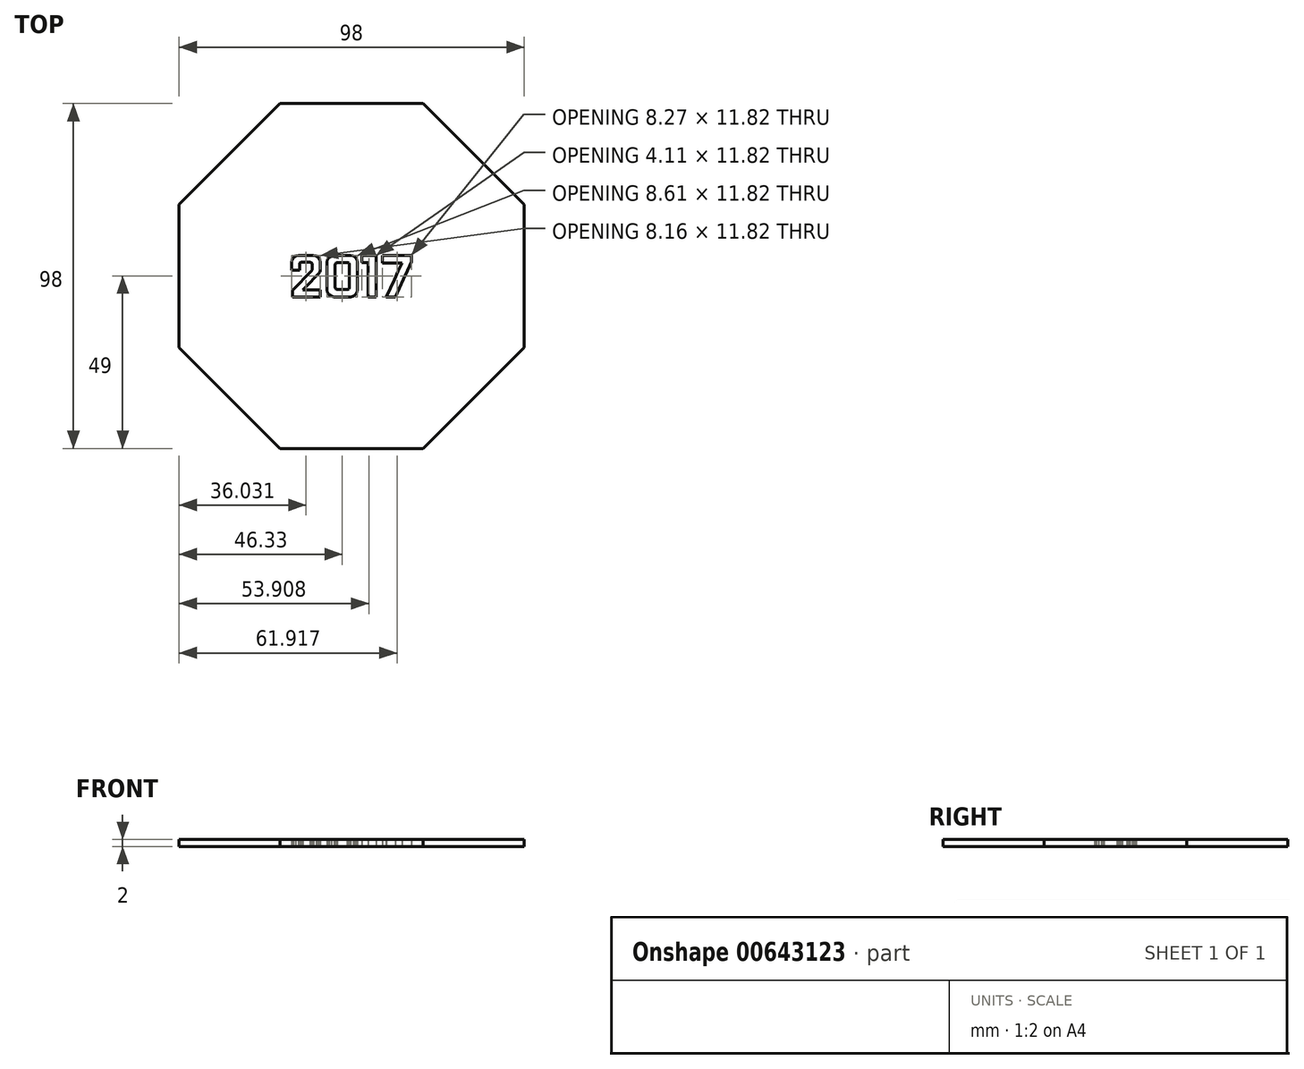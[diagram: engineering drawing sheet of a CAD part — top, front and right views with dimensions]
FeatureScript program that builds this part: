
annotation { "Feature Type Name" : "Feature", "Feature Type Description" : "" }
export const myFeature = defineFeature(function(context is Context, id is Id, definition is map)
    precondition{}
    {
        {
            var Q0;
            Q0=qCreatedBy(makeId("Top.planeOp"),FACE);
            var sketch = newSketch(context, id + "F0", { "sketchPlane" : qUnion([Q0])});
            skLineSegment(sketch, "E0", {"start": v(20.3, 49) * mm, "end": v(-20.3, 49) * mm});
            skLineSegment(sketch, "E1", {"start": v(-20.3, 49) * mm, "end": v(-49, 20.3) * mm});
            skLineSegment(sketch, "E2", {"start": v(-49, 20.3) * mm, "end": v(-49, -20.3) * mm});
            skLineSegment(sketch, "E3", {"start": v(-49, -20.3) * mm, "end": v(-20.3, -49) * mm});
            skLineSegment(sketch, "E4", {"start": v(-20.3, -49) * mm, "end": v(20.3, -49) * mm});
            skLineSegment(sketch, "E5", {"start": v(20.3, -49) * mm, "end": v(49, -20.3) * mm});
            skLineSegment(sketch, "E6", {"start": v(49, -20.3) * mm, "end": v(49, 20.3) * mm});
            skLineSegment(sketch, "E7", {"start": v(49, 20.3) * mm, "end": v(20.3, 49) * mm});
            skLineSegment(sketch, "E8", {"start": v(-17.05, 1.72) * mm, "end": v(-16.48, 1.72) * mm});
            skLineSegment(sketch, "E9", {"start": v(-16.48, 1.72) * mm, "end": v(-15.9, 1.72) * mm});
            skLineSegment(sketch, "E10", {"start": v(-15.9, 1.72) * mm, "end": v(-15.33, 1.72) * mm});
            skLineSegment(sketch, "E11", {"start": v(-15.33, 1.72) * mm, "end": v(-14.76, 1.72) * mm});
            skLineSegment(sketch, "E12", {"start": v(-12.97, 5.9) * mm, "end": v(-14.02, 5.9) * mm});
            skLineSegment(sketch, "E13", {"start": v(-14.02, 5.9) * mm, "end": v(-15.07, 5.9) * mm});
            skLineSegment(sketch, "E14", {"start": v(-15.07, 5.9) * mm, "end": v(-15.84, 5.75) * mm});
            skLineSegment(sketch, "E15", {"start": v(-15.84, 5.75) * mm, "end": v(-16.47, 5.33) * mm});
            skLineSegment(sketch, "E16", {"start": v(-16.47, 5.33) * mm, "end": v(-16.9, 4.7) * mm});
            skLineSegment(sketch, "E17", {"start": v(-16.9, 4.7) * mm, "end": v(-17.05, 3.93) * mm});
            skLineSegment(sketch, "E18", {"start": v(-17.05, 3.93) * mm, "end": v(-17.05, 3.38) * mm});
            skLineSegment(sketch, "E19", {"start": v(-17.05, 3.38) * mm, "end": v(-17.05, 2.82) * mm});
            skLineSegment(sketch, "E20", {"start": v(-17.05, 2.82) * mm, "end": v(-17.05, 2.27) * mm});
            skLineSegment(sketch, "E21", {"start": v(-17.05, 2.27) * mm, "end": v(-17.05, 1.72) * mm});
            skLineSegment(sketch, "E22", {"start": v(-8.89, 2.95) * mm, "end": v(-8.89, 3.44) * mm});
            skLineSegment(sketch, "E23", {"start": v(-8.89, 3.44) * mm, "end": v(-8.89, 3.93) * mm});
            skLineSegment(sketch, "E24", {"start": v(-8.89, 3.93) * mm, "end": v(-9.04, 4.7) * mm});
            skLineSegment(sketch, "E25", {"start": v(-9.04, 4.7) * mm, "end": v(-9.47, 5.33) * mm});
            skLineSegment(sketch, "E26", {"start": v(-9.47, 5.33) * mm, "end": v(-10.1, 5.75) * mm});
            skLineSegment(sketch, "E27", {"start": v(-10.1, 5.75) * mm, "end": v(-10.86, 5.9) * mm});
            skLineSegment(sketch, "E28", {"start": v(-10.86, 5.9) * mm, "end": v(-11.92, 5.9) * mm});
            skLineSegment(sketch, "E29", {"start": v(-11.92, 5.9) * mm, "end": v(-12.97, 5.9) * mm});
            skLineSegment(sketch, "E30", {"start": v(-10, 0.03) * mm, "end": v(-9.58, 0.45) * mm});
            skLineSegment(sketch, "E31", {"start": v(-9.58, 0.45) * mm, "end": v(-9.3, 0.77) * mm});
            skLineSegment(sketch, "E32", {"start": v(-9.3, 0.77) * mm, "end": v(-9.08, 1.14) * mm});
            skLineSegment(sketch, "E33", {"start": v(-9.08, 1.14) * mm, "end": v(-8.94, 1.54) * mm});
            skLineSegment(sketch, "E34", {"start": v(-8.94, 1.54) * mm, "end": v(-8.89, 1.96) * mm});
            skLineSegment(sketch, "E35", {"start": v(-8.89, 1.96) * mm, "end": v(-8.89, 2.45) * mm});
            skLineSegment(sketch, "E36", {"start": v(-8.89, 2.45) * mm, "end": v(-8.89, 2.95) * mm});
            skLineSegment(sketch, "E37", {"start": v(-13.83, -3.9) * mm, "end": v(-12.77, -2.81) * mm});
            skLineSegment(sketch, "E38", {"start": v(-12.77, -2.81) * mm, "end": v(-11.7, -1.72) * mm});
            skLineSegment(sketch, "E39", {"start": v(-11.7, -1.72) * mm, "end": v(-10.64, -0.64) * mm});
            skLineSegment(sketch, "E40", {"start": v(-10.64, -0.64) * mm, "end": v(-10, 0.03) * mm});
            skLineSegment(sketch, "E41", {"start": v(-8.89, -3.9) * mm, "end": v(-10.12, -3.9) * mm});
            skLineSegment(sketch, "E42", {"start": v(-10.12, -3.9) * mm, "end": v(-11.36, -3.9) * mm});
            skLineSegment(sketch, "E43", {"start": v(-11.36, -3.9) * mm, "end": v(-12.6, -3.9) * mm});
            skLineSegment(sketch, "E44", {"start": v(-12.6, -3.9) * mm, "end": v(-13.83, -3.9) * mm});
            skLineSegment(sketch, "E45", {"start": v(-8.89, -5.9) * mm, "end": v(-8.89, -5.4) * mm});
            skLineSegment(sketch, "E46", {"start": v(-8.89, -5.4) * mm, "end": v(-8.89, -4.9) * mm});
            skLineSegment(sketch, "E47", {"start": v(-8.89, -4.9) * mm, "end": v(-8.89, -4.4) * mm});
            skLineSegment(sketch, "E48", {"start": v(-8.89, -4.4) * mm, "end": v(-8.89, -3.9) * mm});
            skLineSegment(sketch, "E49", {"start": v(-16.8, -5.9) * mm, "end": v(-14.81, -5.9) * mm});
            skLineSegment(sketch, "E50", {"start": v(-14.81, -5.9) * mm, "end": v(-12.84, -5.9) * mm});
            skLineSegment(sketch, "E51", {"start": v(-12.84, -5.9) * mm, "end": v(-10.86, -5.9) * mm});
            skLineSegment(sketch, "E52", {"start": v(-10.86, -5.9) * mm, "end": v(-8.89, -5.9) * mm});
            skLineSegment(sketch, "E53", {"start": v(-16.8, -4.02) * mm, "end": v(-16.8, -4.5) * mm});
            skLineSegment(sketch, "E54", {"start": v(-16.8, -4.5) * mm, "end": v(-16.8, -4.97) * mm});
            skLineSegment(sketch, "E55", {"start": v(-16.8, -4.97) * mm, "end": v(-16.8, -5.44) * mm});
            skLineSegment(sketch, "E56", {"start": v(-16.8, -5.44) * mm, "end": v(-16.8, -5.9) * mm});
            skLineSegment(sketch, "E57", {"start": v(-11.18, 2.65) * mm, "end": v(-11.18, 2.32) * mm});
            skLineSegment(sketch, "E58", {"start": v(-11.18, 2.32) * mm, "end": v(-11.18, 2) * mm});
            skLineSegment(sketch, "E59", {"start": v(-11.18, 2) * mm, "end": v(-11.19, 1.87) * mm});
            skLineSegment(sketch, "E60", {"start": v(-11.19, 1.87) * mm, "end": v(-11.23, 1.76) * mm});
            skLineSegment(sketch, "E61", {"start": v(-11.23, 1.76) * mm, "end": v(-11.29, 1.65) * mm});
            skLineSegment(sketch, "E62", {"start": v(-11.29, 1.65) * mm, "end": v(-11.37, 1.56) * mm});
            skLineSegment(sketch, "E63", {"start": v(-11.37, 1.56) * mm, "end": v(-12.72, 0.16) * mm});
            skLineSegment(sketch, "E64", {"start": v(-12.72, 0.16) * mm, "end": v(-14.08, -1.23) * mm});
            skLineSegment(sketch, "E65", {"start": v(-14.08, -1.23) * mm, "end": v(-15.43, -2.63) * mm});
            skLineSegment(sketch, "E66", {"start": v(-15.43, -2.63) * mm, "end": v(-16.8, -4.02) * mm});
            skLineSegment(sketch, "E67", {"start": v(-13.07, 3.9) * mm, "end": v(-12.42, 3.9) * mm});
            skLineSegment(sketch, "E68", {"start": v(-12.42, 3.9) * mm, "end": v(-11.76, 3.9) * mm});
            skLineSegment(sketch, "E69", {"start": v(-11.76, 3.9) * mm, "end": v(-11.53, 3.85) * mm});
            skLineSegment(sketch, "E70", {"start": v(-11.53, 3.85) * mm, "end": v(-11.35, 3.73) * mm});
            skLineSegment(sketch, "E71", {"start": v(-11.35, 3.73) * mm, "end": v(-11.22, 3.54) * mm});
            skLineSegment(sketch, "E72", {"start": v(-11.22, 3.54) * mm, "end": v(-11.18, 3.3) * mm});
            skLineSegment(sketch, "E73", {"start": v(-11.18, 3.3) * mm, "end": v(-11.18, 2.98) * mm});
            skLineSegment(sketch, "E74", {"start": v(-11.18, 2.98) * mm, "end": v(-11.18, 2.65) * mm});
            skLineSegment(sketch, "E75", {"start": v(-14.76, 1.72) * mm, "end": v(-14.76, 2.16) * mm});
            skLineSegment(sketch, "E76", {"start": v(-14.76, 2.16) * mm, "end": v(-14.76, 2.6) * mm});
            skLineSegment(sketch, "E77", {"start": v(-14.76, 2.6) * mm, "end": v(-14.76, 3.05) * mm});
            skLineSegment(sketch, "E78", {"start": v(-14.76, 3.05) * mm, "end": v(-14.76, 3.5) * mm});
            skLineSegment(sketch, "E79", {"start": v(-14.76, 3.5) * mm, "end": v(-14.73, 3.66) * mm});
            skLineSegment(sketch, "E80", {"start": v(-14.73, 3.66) * mm, "end": v(-14.65, 3.78) * mm});
            skLineSegment(sketch, "E81", {"start": v(-14.65, 3.78) * mm, "end": v(-14.53, 3.87) * mm});
            skLineSegment(sketch, "E82", {"start": v(-14.53, 3.87) * mm, "end": v(-14.38, 3.9) * mm});
            skLineSegment(sketch, "E83", {"start": v(-14.38, 3.9) * mm, "end": v(-13.73, 3.9) * mm});
            skLineSegment(sketch, "E84", {"start": v(-13.73, 3.9) * mm, "end": v(-13.07, 3.9) * mm});
            skLineSegment(sketch, "E85", {"start": v(-4.69, -3.22) * mm, "end": v(-4.69, -1.61) * mm});
            skLineSegment(sketch, "E86", {"start": v(-4.69, -1.61) * mm, "end": v(-4.69, 0) * mm});
            skLineSegment(sketch, "E87", {"start": v(-4.69, 0) * mm, "end": v(-4.69, 1.61) * mm});
            skLineSegment(sketch, "E88", {"start": v(-4.69, 1.61) * mm, "end": v(-4.69, 3.22) * mm});
            skLineSegment(sketch, "E89", {"start": v(-4.69, 3.22) * mm, "end": v(-4.64, 3.45) * mm});
            skLineSegment(sketch, "E90", {"start": v(-4.64, 3.45) * mm, "end": v(-4.51, 3.63) * mm});
            skLineSegment(sketch, "E91", {"start": v(-4.51, 3.63) * mm, "end": v(-4.32, 3.76) * mm});
            skLineSegment(sketch, "E92", {"start": v(-4.32, 3.76) * mm, "end": v(-4.1, 3.81) * mm});
            skLineSegment(sketch, "E93", {"start": v(-4.1, 3.81) * mm, "end": v(-3.38, 3.81) * mm});
            skLineSegment(sketch, "E94", {"start": v(-3.38, 3.81) * mm, "end": v(-2.67, 3.81) * mm});
            skLineSegment(sketch, "E95", {"start": v(-2.67, 3.81) * mm, "end": v(-1.96, 3.81) * mm});
            skLineSegment(sketch, "E96", {"start": v(-1.96, 3.81) * mm, "end": v(-1.24, 3.81) * mm});
            skLineSegment(sketch, "E97", {"start": v(-1.24, 3.81) * mm, "end": v(-1, 3.76) * mm});
            skLineSegment(sketch, "E98", {"start": v(-1, 3.76) * mm, "end": v(-0.82, 3.63) * mm});
            skLineSegment(sketch, "E99", {"start": v(-0.82, 3.63) * mm, "end": v(-0.7, 3.45) * mm});
            skLineSegment(sketch, "E100", {"start": v(-0.7, 3.45) * mm, "end": v(-0.65, 3.22) * mm});
            skLineSegment(sketch, "E101", {"start": v(-0.65, 3.22) * mm, "end": v(-0.65, 1.61) * mm});
            skLineSegment(sketch, "E102", {"start": v(-0.65, 1.61) * mm, "end": v(-0.65, 0) * mm});
            skLineSegment(sketch, "E103", {"start": v(-0.65, 0) * mm, "end": v(-0.65, -1.61) * mm});
            skLineSegment(sketch, "E104", {"start": v(-0.65, -1.61) * mm, "end": v(-0.65, -3.22) * mm});
            skLineSegment(sketch, "E105", {"start": v(-0.65, -3.22) * mm, "end": v(-0.7, -3.45) * mm});
            skLineSegment(sketch, "E106", {"start": v(-0.7, -3.45) * mm, "end": v(-0.82, -3.64) * mm});
            skLineSegment(sketch, "E107", {"start": v(-0.82, -3.64) * mm, "end": v(-1, -3.77) * mm});
            skLineSegment(sketch, "E108", {"start": v(-1, -3.77) * mm, "end": v(-1.24, -3.81) * mm});
            skLineSegment(sketch, "E109", {"start": v(-1.24, -3.81) * mm, "end": v(-1.96, -3.81) * mm});
            skLineSegment(sketch, "E110", {"start": v(-1.96, -3.81) * mm, "end": v(-2.67, -3.81) * mm});
            skLineSegment(sketch, "E111", {"start": v(-2.67, -3.81) * mm, "end": v(-3.38, -3.81) * mm});
            skLineSegment(sketch, "E112", {"start": v(-3.38, -3.81) * mm, "end": v(-4.1, -3.81) * mm});
            skLineSegment(sketch, "E113", {"start": v(-4.1, -3.81) * mm, "end": v(-4.32, -3.77) * mm});
            skLineSegment(sketch, "E114", {"start": v(-4.32, -3.77) * mm, "end": v(-4.51, -3.64) * mm});
            skLineSegment(sketch, "E115", {"start": v(-4.51, -3.64) * mm, "end": v(-4.64, -3.45) * mm});
            skLineSegment(sketch, "E116", {"start": v(-4.64, -3.45) * mm, "end": v(-4.69, -3.22) * mm});
            skLineSegment(sketch, "E117", {"start": v(1.64, 3.93) * mm, "end": v(1.48, 4.7) * mm});
            skLineSegment(sketch, "E118", {"start": v(1.48, 4.7) * mm, "end": v(1.06, 5.33) * mm});
            skLineSegment(sketch, "E119", {"start": v(1.06, 5.33) * mm, "end": v(0.44, 5.75) * mm});
            skLineSegment(sketch, "E120", {"start": v(0.44, 5.75) * mm, "end": v(-0.32, 5.9) * mm});
            skLineSegment(sketch, "E121", {"start": v(-0.32, 5.9) * mm, "end": v(-1.5, 5.9) * mm});
            skLineSegment(sketch, "E122", {"start": v(-1.5, 5.9) * mm, "end": v(-2.66, 5.9) * mm});
            skLineSegment(sketch, "E123", {"start": v(-2.66, 5.9) * mm, "end": v(-3.83, 5.9) * mm});
            skLineSegment(sketch, "E124", {"start": v(-3.83, 5.9) * mm, "end": v(-5, 5.9) * mm});
            skLineSegment(sketch, "E125", {"start": v(-5, 5.9) * mm, "end": v(-5.77, 5.75) * mm});
            skLineSegment(sketch, "E126", {"start": v(-5.77, 5.75) * mm, "end": v(-6.4, 5.33) * mm});
            skLineSegment(sketch, "E127", {"start": v(-6.4, 5.33) * mm, "end": v(-6.82, 4.7) * mm});
            skLineSegment(sketch, "E128", {"start": v(-6.82, 4.7) * mm, "end": v(-6.98, 3.93) * mm});
            skLineSegment(sketch, "E129", {"start": v(-6.98, 3.93) * mm, "end": v(-6.98, 3) * mm});
            skLineSegment(sketch, "E130", {"start": v(1.64, -3.95) * mm, "end": v(1.64, -1.98) * mm});
            skLineSegment(sketch, "E131", {"start": v(1.64, -1.98) * mm, "end": v(1.64, 0) * mm});
            skLineSegment(sketch, "E132", {"start": v(1.64, 0) * mm, "end": v(1.64, 1.96) * mm});
            skLineSegment(sketch, "E133", {"start": v(1.64, 1.96) * mm, "end": v(1.64, 3.93) * mm});
            skLineSegment(sketch, "E134", {"start": v(-6.98, -3.95) * mm, "end": v(-6.82, -4.72) * mm});
            skLineSegment(sketch, "E135", {"start": v(-6.82, -4.72) * mm, "end": v(-6.4, -5.34) * mm});
            skLineSegment(sketch, "E136", {"start": v(-6.4, -5.34) * mm, "end": v(-5.77, -5.76) * mm});
            skLineSegment(sketch, "E137", {"start": v(-5.77, -5.76) * mm, "end": v(-5, -5.9) * mm});
            skLineSegment(sketch, "E138", {"start": v(-5, -5.9) * mm, "end": v(-3.83, -5.9) * mm});
            skLineSegment(sketch, "E139", {"start": v(-3.83, -5.9) * mm, "end": v(-2.66, -5.9) * mm});
            skLineSegment(sketch, "E140", {"start": v(-2.66, -5.9) * mm, "end": v(-1.5, -5.9) * mm});
            skLineSegment(sketch, "E141", {"start": v(-1.5, -5.9) * mm, "end": v(-0.32, -5.9) * mm});
            skLineSegment(sketch, "E142", {"start": v(-0.32, -5.9) * mm, "end": v(0.44, -5.76) * mm});
            skLineSegment(sketch, "E143", {"start": v(0.44, -5.76) * mm, "end": v(1.06, -5.34) * mm});
            skLineSegment(sketch, "E144", {"start": v(1.06, -5.34) * mm, "end": v(1.48, -4.72) * mm});
            skLineSegment(sketch, "E145", {"start": v(1.48, -4.72) * mm, "end": v(1.64, -3.95) * mm});
            skLineSegment(sketch, "E146", {"start": v(-6.98, 3) * mm, "end": v(-6.98, 1.96) * mm});
            skLineSegment(sketch, "E147", {"start": v(-6.98, 1.96) * mm, "end": v(-6.98, 0) * mm});
            skLineSegment(sketch, "E148", {"start": v(-6.98, 0) * mm, "end": v(-6.98, -1.98) * mm});
            skLineSegment(sketch, "E149", {"start": v(-6.98, -1.98) * mm, "end": v(-6.98, -3.95) * mm});
            skLineSegment(sketch, "E150", {"start": v(2.85, 5.9) * mm, "end": v(2.85, 5.39) * mm});
            skLineSegment(sketch, "E151", {"start": v(2.85, 5.39) * mm, "end": v(2.85, 4.87) * mm});
            skLineSegment(sketch, "E152", {"start": v(2.85, 4.87) * mm, "end": v(2.85, 4.35) * mm});
            skLineSegment(sketch, "E153", {"start": v(2.85, 4.35) * mm, "end": v(2.85, 3.83) * mm});
            skLineSegment(sketch, "E154", {"start": v(2.85, 3.83) * mm, "end": v(3.3, 3.83) * mm});
            skLineSegment(sketch, "E155", {"start": v(3.3, 3.83) * mm, "end": v(3.76, 3.83) * mm});
            skLineSegment(sketch, "E156", {"start": v(3.76, 3.83) * mm, "end": v(4.22, 3.83) * mm});
            skLineSegment(sketch, "E157", {"start": v(4.22, 3.83) * mm, "end": v(4.67, 3.83) * mm});
            skLineSegment(sketch, "E158", {"start": v(4.67, 3.83) * mm, "end": v(4.67, 1.4) * mm});
            skLineSegment(sketch, "E159", {"start": v(4.67, 1.4) * mm, "end": v(4.67, -1.04) * mm});
            skLineSegment(sketch, "E160", {"start": v(4.67, -1.04) * mm, "end": v(4.67, -3.47) * mm});
            skLineSegment(sketch, "E161", {"start": v(4.67, -3.47) * mm, "end": v(4.67, -5.9) * mm});
            skLineSegment(sketch, "E162", {"start": v(4.67, -5.9) * mm, "end": v(5.25, -5.9) * mm});
            skLineSegment(sketch, "E163", {"start": v(5.25, -5.9) * mm, "end": v(5.82, -5.9) * mm});
            skLineSegment(sketch, "E164", {"start": v(5.82, -5.9) * mm, "end": v(6.39, -5.9) * mm});
            skLineSegment(sketch, "E165", {"start": v(6.39, -5.9) * mm, "end": v(6.96, -5.9) * mm});
            skLineSegment(sketch, "E166", {"start": v(6.96, -5.9) * mm, "end": v(6.96, -2.95) * mm});
            skLineSegment(sketch, "E167", {"start": v(6.96, -2.95) * mm, "end": v(6.96, 0) * mm});
            skLineSegment(sketch, "E168", {"start": v(6.96, 0) * mm, "end": v(6.96, 2.95) * mm});
            skLineSegment(sketch, "E169", {"start": v(6.96, 2.95) * mm, "end": v(6.96, 5.9) * mm});
            skLineSegment(sketch, "E170", {"start": v(6.96, 5.9) * mm, "end": v(5.93, 5.9) * mm});
            skLineSegment(sketch, "E171", {"start": v(5.93, 5.9) * mm, "end": v(4.9, 5.9) * mm});
            skLineSegment(sketch, "E172", {"start": v(4.9, 5.9) * mm, "end": v(3.88, 5.9) * mm});
            skLineSegment(sketch, "E173", {"start": v(3.88, 5.9) * mm, "end": v(2.85, 5.9) * mm});
            skLineSegment(sketch, "E174", {"start": v(8.78, 5.9) * mm, "end": v(8.78, 5.37) * mm});
            skLineSegment(sketch, "E175", {"start": v(8.78, 5.37) * mm, "end": v(8.78, 4.83) * mm});
            skLineSegment(sketch, "E176", {"start": v(8.78, 4.83) * mm, "end": v(8.78, 4.28) * mm});
            skLineSegment(sketch, "E177", {"start": v(8.78, 4.28) * mm, "end": v(8.78, 3.74) * mm});
            skLineSegment(sketch, "E178", {"start": v(8.78, 3.74) * mm, "end": v(10.18, 3.74) * mm});
            skLineSegment(sketch, "E179", {"start": v(10.18, 3.74) * mm, "end": v(11.57, 3.74) * mm});
            skLineSegment(sketch, "E180", {"start": v(11.57, 3.74) * mm, "end": v(12.97, 3.74) * mm});
            skLineSegment(sketch, "E181", {"start": v(12.97, 3.74) * mm, "end": v(14.36, 3.74) * mm});
            skLineSegment(sketch, "E182", {"start": v(14.36, 3.74) * mm, "end": v(13.25, 1.34) * mm});
            skLineSegment(sketch, "E183", {"start": v(13.25, 1.34) * mm, "end": v(12.13, -1.07) * mm});
            skLineSegment(sketch, "E184", {"start": v(12.13, -1.07) * mm, "end": v(11.01, -3.47) * mm});
            skLineSegment(sketch, "E185", {"start": v(11.01, -3.47) * mm, "end": v(9.9, -5.88) * mm});
            skLineSegment(sketch, "E186", {"start": v(9.9, -5.88) * mm, "end": v(9.85, -5.88) * mm});
            skLineSegment(sketch, "E187", {"start": v(9.85, -5.88) * mm, "end": v(9.8, -5.9) * mm});
            skLineSegment(sketch, "E188", {"start": v(9.8, -5.9) * mm, "end": v(9.76, -5.9) * mm});
            skLineSegment(sketch, "E189", {"start": v(9.76, -5.9) * mm, "end": v(9.72, -5.9) * mm});
            skLineSegment(sketch, "E190", {"start": v(9.72, -5.9) * mm, "end": v(10.4, -5.9) * mm});
            skLineSegment(sketch, "E191", {"start": v(10.4, -5.9) * mm, "end": v(11.1, -5.9) * mm});
            skLineSegment(sketch, "E192", {"start": v(11.1, -5.9) * mm, "end": v(11.79, -5.9) * mm});
            skLineSegment(sketch, "E193", {"start": v(11.79, -5.9) * mm, "end": v(12.48, -5.9) * mm});
            skLineSegment(sketch, "E194", {"start": v(12.48, -5.9) * mm, "end": v(13.62, -3.4) * mm});
            skLineSegment(sketch, "E195", {"start": v(13.62, -3.4) * mm, "end": v(14.76, -0.9) * mm});
            skLineSegment(sketch, "E196", {"start": v(14.76, -0.9) * mm, "end": v(15.9, 1.59) * mm});
            skLineSegment(sketch, "E197", {"start": v(15.9, 1.59) * mm, "end": v(17.05, 4.09) * mm});
            skLineSegment(sketch, "E198", {"start": v(17.05, 4.09) * mm, "end": v(17.05, 4.54) * mm});
            skLineSegment(sketch, "E199", {"start": v(17.05, 4.54) * mm, "end": v(17.05, 5) * mm});
            skLineSegment(sketch, "E200", {"start": v(17.05, 5) * mm, "end": v(17.05, 5.45) * mm});
            skLineSegment(sketch, "E201", {"start": v(17.05, 5.45) * mm, "end": v(17.05, 5.9) * mm});
            skLineSegment(sketch, "E202", {"start": v(17.05, 5.9) * mm, "end": v(14.98, 5.9) * mm});
            skLineSegment(sketch, "E203", {"start": v(14.98, 5.9) * mm, "end": v(12.92, 5.9) * mm});
            skLineSegment(sketch, "E204", {"start": v(12.92, 5.9) * mm, "end": v(10.85, 5.9) * mm});
            skLineSegment(sketch, "E205", {"start": v(10.85, 5.9) * mm, "end": v(8.78, 5.9) * mm});
            skSolve(sketch);
        }
        {
            var Q0;
            Q0=makeQuery(id+"F0.imprint","IMPRINT",FACE,{"disambiguationData":[TD([[makeQuery(id+"F0.imprint","IMPRINT",EDGE,{"derivedFrom":sQuery(id+"F0.wireOp",EDGE,"E0")}),1.0]])]});
            var Q1;
            Q1=makeQuery(id+"F0.imprint","IMPRINT",FACE,{"disambiguationData":[TD([[makeQuery(id+"F0.imprint","IMPRINT",EDGE,{"derivedFrom":sQuery(id+"F0.wireOp",EDGE,"E85")}),-1.0]])]});
            extrude(context, id + "F1", {"entities" : qUnion([Q0, Q1]), "depth" : 2 * mm, "offsetDistance" : 25 * mm});
        }
    });
